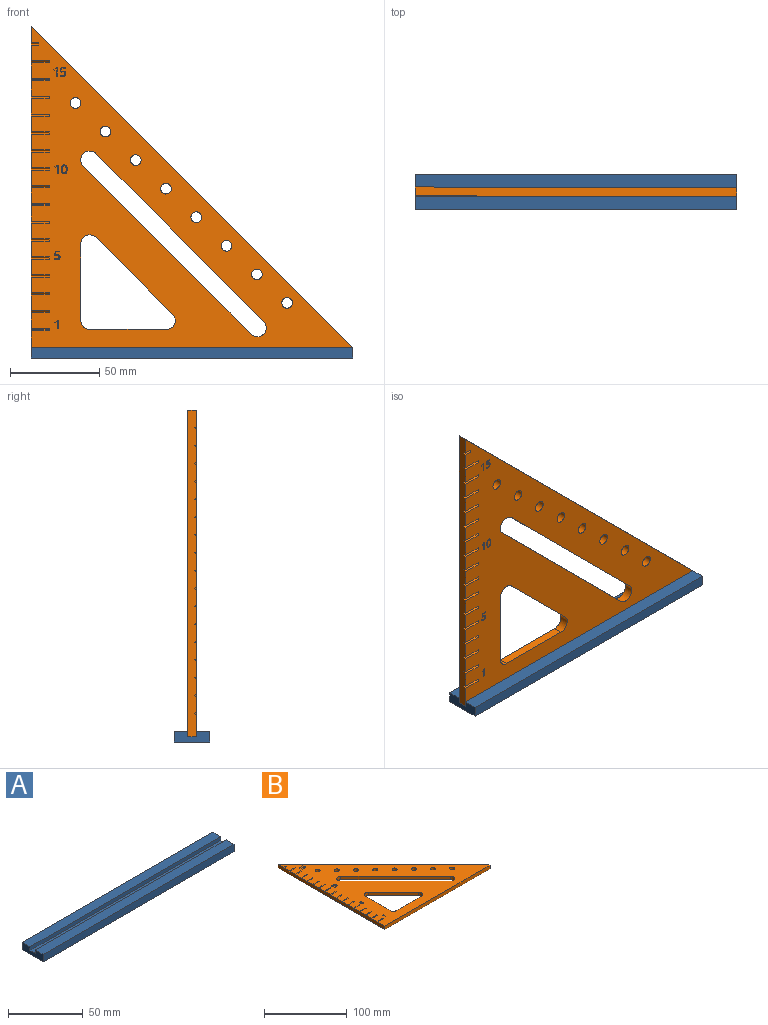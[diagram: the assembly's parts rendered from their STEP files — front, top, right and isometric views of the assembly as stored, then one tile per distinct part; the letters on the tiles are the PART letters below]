
ASSEMBLY  parts=2 mates=1
PART A: 10 faces, bbox 180x20x6 mm
  f0: plane 180x20mm, normal (0,0,-1), area 3600mm2, adj f1,f7,f8,f9
  f1: plane 180x6mm, normal (0,1,0), area 1080mm2, adj f0,f2,f8,f9
  f2: plane 180x7.5mm, normal (0,0,1), area 1350mm2, adj f1,f3,f8,f9
  f3: plane 180x3mm, normal (0,-1,0), area 540mm2, adj f2,f4,f8,f9
  f4: plane 180x5mm, normal (0,0,1), area 900mm2, adj f3,f5,f8,f9
  f5: plane 180x3mm, normal (0,1,0), area 540mm2, adj f4,f6,f8,f9
  f6: plane 180x7.5mm, normal (0,0,1), area 1350mm2, adj f5,f7,f8,f9
  f7: plane 180x6mm, normal (0,-1,0), area 1080mm2, adj f0,f6,f8,f9
  f8: plane 20x6mm, normal (1,0,0), area 105mm2, adj f0,f1,f2,f3,f4,f5,f6,f7
  f9: plane 20x6mm, normal (-1,0,0), area 105mm2, adj f0,f1,f2,f3,f4,f5,f6,f7
PART B: 164 faces, bbox 180x183x5 mm
  f0: plane 183x180mm, normal (0,0,1), area 13110.9mm2, adj f1,f2,f3,f4,f5,f6,f7,f8
  f1: plane 183x5mm, normal (-1,0,0), area 899.5mm2, adj f0,f12,f14,f16,f17,f18,f20,f21
  f2: cylinder r=5mm len=8.54mm, axis (0,0,-1), area 58.9mm2, adj f0,f3,f15,f16
  f3: plane 42.93x5mm, normal (0,1,0), area 214.6mm2, adj f0,f2,f4,f16
  f4: cylinder r=5mm len=5mm, axis (0,0,-1), area 39.3mm2, adj f0,f3,f5,f16
  f5: plane 42.93x5mm, normal (1,0,0), area 214.6mm2, adj f0,f4,f6,f16
  f6: cylinder r=5mm len=8.54mm, axis (0,0,-1), area 58.9mm2, adj f0,f5,f15,f16
  f7: plane 94.05x94.05mm, normal (0.71,0.71,0), area 665mm2, adj f0,f8,f13,f16
  f8: cylinder r=5mm len=8.54mm, axis (0,0,-1), area 78.5mm2, adj f0,f7,f9,f16
  f9: plane 94.05x94.05mm, normal (-0.71,-0.71,0), area 665mm2, adj f0,f8,f13,f16
  f10: plane 5x3mm, normal (1,0,0), area 15mm2, adj f0,f11,f14,f16
  f11: plane 5x0mm, normal (0,-1,0), area 0mm2, adj f0,f10,f12,f16
  f12: plane 180x180mm, normal (0.71,0.71,0), area 1272.8mm2, adj f0,f1,f11,f16
  f13: cylinder r=5mm len=8.54mm, axis (0,0,-1), area 78.5mm2, adj f0,f7,f9,f16
  f14: plane 180x5mm, normal (0,-1,0), area 900mm2, adj f0,f1,f10,f16
  f15: plane 42.93x42.93mm, normal (-0.71,-0.71,0), area 303.6mm2, adj f0,f2,f6,f16
  f16: plane 183x180mm, normal (0,0,-1), area 13372.4mm2, adj f1,f2,f3,f4,f5,f6,f7,f8
  f17: plane 10x1.31mm, normal (0,-0.88,0.47), area 14.9mm2, adj f0,f1,f18,f19
  f18: plane 10x1.31mm, normal (0,0.88,0.47), area 14.9mm2, adj f0,f1,f17,f19
  f19: plane 1.39x1.31mm, normal (-1,0,0), area 0.9mm2, adj f0,f17,f18
  f20: plane 10x1.31mm, normal (0,-0.88,0.47), area 14.9mm2, adj f0,f1,f21,f22
  f21: plane 10x1.31mm, normal (0,0.88,0.47), area 14.9mm2, adj f0,f1,f20,f22
  f22: plane 1.39x1.31mm, normal (-1,0,0), area 0.9mm2, adj f0,f20,f21
  f23: plane 10x1.31mm, normal (0,-0.88,0.47), area 14.9mm2, adj f0,f1,f24,f25
  f24: plane 10x1.31mm, normal (0,0.88,0.47), area 14.9mm2, adj f0,f1,f23,f25
  f25: plane 1.39x1.31mm, normal (-1,0,0), area 0.9mm2, adj f0,f23,f24
  f26: plane 10x1.31mm, normal (0,-0.88,0.47), area 14.9mm2, adj f0,f1,f27,f28
  f27: plane 10x1.31mm, normal (0,0.88,0.47), area 14.9mm2, adj f0,f1,f26,f28
  f28: plane 1.39x1.31mm, normal (-1,0,0), area 0.9mm2, adj f0,f26,f27
  f29: plane 10x1.31mm, normal (0,-0.88,0.47), area 14.9mm2, adj f0,f1,f30,f31
  f30: plane 10x1.31mm, normal (0,0.88,0.47), area 14.9mm2, adj f0,f1,f29,f31
  f31: plane 1.39x1.31mm, normal (-1,0,0), area 0.9mm2, adj f0,f29,f30
  f32: plane 10x1.31mm, normal (0,-0.88,0.47), area 14.9mm2, adj f0,f1,f33,f34
  f33: plane 10x1.31mm, normal (0,0.88,0.47), area 14.9mm2, adj f0,f1,f32,f34
  f34: plane 1.39x1.31mm, normal (-1,0,0), area 0.9mm2, adj f0,f32,f33
  f35: plane 10x1.31mm, normal (0,-0.88,0.47), area 14.9mm2, adj f0,f1,f36,f37
  f36: plane 10x1.31mm, normal (0,0.88,0.47), area 14.9mm2, adj f0,f1,f35,f37
  f37: plane 1.39x1.31mm, normal (-1,0,0), area 0.9mm2, adj f0,f35,f36
  f38: plane 10x1.31mm, normal (0,-0.88,0.47), area 14.9mm2, adj f0,f1,f39,f40
  f39: plane 10x1.31mm, normal (0,0.88,0.47), area 14.9mm2, adj f0,f1,f38,f40
  f40: plane 1.39x1.31mm, normal (-1,0,0), area 0.9mm2, adj f0,f38,f39
  f41: plane 10x1.31mm, normal (0,-0.88,0.47), area 14.9mm2, adj f0,f1,f42,f43
  f42: plane 10x1.31mm, normal (0,0.88,0.47), area 14.9mm2, adj f0,f1,f41,f43
  f43: plane 1.39x1.31mm, normal (-1,0,0), area 0.9mm2, adj f0,f41,f42
  f44: plane 10x1.31mm, normal (0,-0.88,0.47), area 14.9mm2, adj f0,f1,f45,f46
  f45: plane 10x1.31mm, normal (0,0.88,0.47), area 14.9mm2, adj f0,f1,f44,f46
  f46: plane 1.39x1.31mm, normal (-1,0,0), area 0.9mm2, adj f0,f44,f45
  f47: plane 10x1.31mm, normal (0,-0.88,0.47), area 14.9mm2, adj f0,f1,f48,f49
  f48: plane 10x1.31mm, normal (0,0.88,0.47), area 14.9mm2, adj f0,f1,f47,f49
  f49: plane 1.39x1.31mm, normal (-1,0,0), area 0.9mm2, adj f0,f47,f48
  f50: plane 10x1.31mm, normal (0,-0.88,0.47), area 14.9mm2, adj f0,f1,f51,f52
  f51: plane 10x1.31mm, normal (0,0.88,0.47), area 14.9mm2, adj f0,f1,f50,f52
  f52: plane 1.39x1.31mm, normal (-1,0,0), area 0.9mm2, adj f0,f50,f51
  f53: plane 10x1.31mm, normal (0,-0.88,0.47), area 14.9mm2, adj f0,f1,f54,f55
  f54: plane 10x1.31mm, normal (0,0.88,0.47), area 14.9mm2, adj f0,f1,f53,f55
  f55: plane 1.39x1.31mm, normal (-1,0,0), area 0.9mm2, adj f0,f53,f54
  f56: plane 10x1.31mm, normal (0,-0.88,0.47), area 14.9mm2, adj f0,f1,f57,f58
  f57: plane 10x1.31mm, normal (0,0.88,0.47), area 14.9mm2, adj f0,f1,f56,f58
  f58: plane 1.39x1.31mm, normal (-1,0,0), area 0.9mm2, adj f0,f56,f57
  f59: plane 10x1.31mm, normal (0,-0.88,0.47), area 14.9mm2, adj f0,f1,f60,f61
  f60: plane 10x1.31mm, normal (0,0.88,0.47), area 14.9mm2, adj f0,f1,f59,f61
  f61: plane 1.39x1.31mm, normal (-1,0,0), area 0.9mm2, adj f0,f59,f60
  f62: plane 10x1.31mm, normal (0,0.88,0.47), area 14.9mm2, adj f0,f1,f63,f64
  f63: plane 10x1.31mm, normal (0,-0.88,0.47), area 14.9mm2, adj f0,f1,f62,f64
  f64: plane 1.39x1.31mm, normal (-1,0,0), area 0.9mm2, adj f0,f62,f63
  f65: plane 4x1.31mm, normal (0,-0.88,0.47), area 5.9mm2, adj f0,f1,f66,f67
  f66: plane 4x1.31mm, normal (0,0.88,0.47), area 5.9mm2, adj f0,f1,f65,f67
  f67: plane 1.39x1.31mm, normal (-1,0,0), area 0.9mm2, adj f0,f65,f66
  f68: cylinder r=3mm len=6mm, axis (0,0,1), area 94.2mm2, adj f0,f16
  f69: extruded ~1.86x1mm, area 1.9mm2, adj f0,f70,f84,f85
  f70: extruded ~1.2x1mm, area 1.4mm2, adj f0,f69,f71,f85
  f71: extruded ~1.21x1mm, area 1.4mm2, adj f0,f70,f72,f85
  f72: extruded ~1.89x1mm, area 2mm2, adj f0,f71,f73,f85
  f73: extruded ~1.87x1mm, area 1.9mm2, adj f0,f72,f74,f85
  f74: extruded ~1.2x1mm, area 1.4mm2, adj f0,f73,f75,f85
  f75: extruded ~1.22x1mm, area 1.4mm2, adj f0,f74,f84,f85
  f76: extruded ~1.54x1mm, area 1.6mm2, adj f77,f83,f85,f86
  f77: extruded ~1x0.8mm, area 1mm2, adj f76,f78,f85,f86
  f78: extruded ~1x0.8mm, area 1mm2, adj f77,f79,f85,f86
  f79: extruded ~1.54x1mm, area 1.6mm2, adj f78,f80,f85,f86
  f80: extruded ~1.54x1mm, area 1.6mm2, adj f79,f81,f85,f86
  f81: extruded ~1x0.8mm, area 1mm2, adj f80,f82,f85,f86
  f82: extruded ~1x0.8mm, area 1mm2, adj f81,f83,f85,f86
  f83: extruded ~1.55x1mm, area 1.6mm2, adj f76,f82,f85,f86
  f84: extruded ~1.89x1mm, area 2mm2, adj f0,f69,f75,f85
  f85: plane 5.01x3.22mm, normal (0,0,1), area 6.3mm2, adj f69,f70,f71,f72,f73,f74,f75,f76
  f86: plane 4.06x2.09mm, normal (0,0,1), area 7.2mm2, adj f76,f77,f78,f79,f80,f81,f82,f83
  f87: extruded ~1x0.76mm, area 0.8mm2, adj f0,f88,f105,f106
  f88: plane 1.46x1mm, normal (-1,0.08,0), area 1.5mm2, adj f0,f87,f89,f106
  f89: plane 1.95x1mm, normal (0,1,0), area 1.9mm2, adj f0,f88,f90,f106
  f90: plane 1x0.51mm, normal (-1,0,0), area 0.5mm2, adj f0,f89,f91,f106
  f91: plane 2.42x1mm, normal (0,-1,0), area 2.4mm2, adj f0,f90,f92,f106
  f92: plane 2.28x1mm, normal (1,-0.08,0), area 2.3mm2, adj f0,f91,f93,f106
  f93: plane 1x0.29mm, normal (0.54,0.84,0), area 0.3mm2, adj f0,f92,f94,f106
  f94: extruded ~1x0.85mm, area 0.9mm2, adj f0,f93,f95,f106
  f95: extruded ~1.25x1.02mm, area 1.8mm2, adj f0,f94,f96,f106
  f96: extruded ~1x0.8mm, area 0.9mm2, adj f0,f95,f97,f106
  f97: extruded ~1x0.91mm, area 1mm2, adj f0,f96,f98,f106
  f98: extruded ~1x0.68mm, area 0.7mm2, adj f0,f97,f99,f106
  f99: extruded ~1x0.58mm, area 0.6mm2, adj f0,f98,f100,f106
  f100: plane 1x0.53mm, normal (1,0,0), area 0.5mm2, adj f0,f99,f101,f106
  f101: extruded ~1.26x1mm, area 1.3mm2, adj f0,f100,f102,f106
  f102: extruded ~1.33x1mm, area 1.4mm2, adj f0,f101,f103,f106
  f103: extruded ~1.19x1mm, area 1.3mm2, adj f0,f102,f104,f106
  f104: extruded ~1.04x1mm, area 1.2mm2, adj f0,f103,f105,f106
  f105: extruded ~1.21x1mm, area 1.3mm2, adj f0,f87,f104,f106
  f106: plane 4.94x3.06mm, normal (0,0,1), area 5.5mm2, adj f87,f88,f89,f90,f91,f92,f93,f94
  f107: plane 4.87x1mm, normal (-1,0,0), area 4.9mm2, adj f0,f108,f115,f116
  f108: plane 1x0.47mm, normal (0,-1,0), area 0.5mm2, adj f0,f107,f109,f116
  f109: plane 1.29x1mm, normal (0.61,-0.79,0), area 1.6mm2, adj f0,f108,f110,f116
  f110: plane 1x0.38mm, normal (0.79,0.61,0), area 0.5mm2, adj f0,f109,f111,f116
  f111: extruded ~1x0.79mm, area 1mm2, adj f0,f110,f112,f116
  f112: extruded ~1x0.16mm, area 0.2mm2, adj f0,f111,f113,f116
  f113: extruded ~1x0.82mm, area 0.8mm2, adj f0,f112,f114,f116
  f114: plane 3.47x1mm, normal (1,0,0), area 3.5mm2, adj f0,f113,f115,f116
  f115: plane 1x0.54mm, normal (0,1,0), area 0.5mm2, adj f0,f107,f114,f116
  f116: plane 4.87x1.75mm, normal (0,0,1), area 3.2mm2, adj f107,f108,f109,f110,f111,f112,f113,f114
  f117: plane 4.87x1mm, normal (-1,0,0), area 4.9mm2, adj f0,f118,f125,f126
  f118: plane 1x0.47mm, normal (0,-1,0), area 0.5mm2, adj f0,f117,f119,f126
  f119: plane 1.29x1mm, normal (0.61,-0.79,0), area 1.6mm2, adj f0,f118,f120,f126
  f120: plane 1x0.38mm, normal (0.79,0.61,0), area 0.5mm2, adj f0,f119,f121,f126
  f121: extruded ~1x0.79mm, area 1mm2, adj f0,f120,f122,f126
  f122: extruded ~1x0.16mm, area 0.2mm2, adj f0,f121,f123,f126
  f123: extruded ~1x0.82mm, area 0.8mm2, adj f0,f122,f124,f126
  f124: plane 3.47x1mm, normal (1,0,0), area 3.5mm2, adj f0,f123,f125,f126
  f125: plane 1x0.54mm, normal (0,1,0), area 0.5mm2, adj f0,f117,f124,f126
  f126: plane 4.87x1.75mm, normal (0,0,1), area 3.2mm2, adj f117,f118,f119,f120,f121,f122,f123,f124
  f127: extruded ~1x0.76mm, area 0.8mm2, adj f0,f128,f145,f146
  f128: plane 1.46x1mm, normal (-1,0.08,0), area 1.5mm2, adj f0,f127,f129,f146
  f129: plane 1.95x1mm, normal (0,1,0), area 1.9mm2, adj f0,f128,f130,f146
  f130: plane 1x0.51mm, normal (-1,0,0), area 0.5mm2, adj f0,f129,f131,f146
  f131: plane 2.42x1mm, normal (0,-1,0), area 2.4mm2, adj f0,f130,f132,f146
  f132: plane 2.28x1mm, normal (1,-0.08,0), area 2.3mm2, adj f0,f131,f133,f146
  f133: plane 1x0.29mm, normal (0.54,0.84,0), area 0.3mm2, adj f0,f132,f134,f146
  f134: extruded ~1x0.85mm, area 0.9mm2, adj f0,f133,f135,f146
  f135: extruded ~1.25x1.02mm, area 1.8mm2, adj f0,f134,f136,f146
  f136: extruded ~1x0.8mm, area 0.9mm2, adj f0,f135,f137,f146
  f137: extruded ~1x0.91mm, area 1mm2, adj f0,f136,f138,f146
  f138: extruded ~1x0.68mm, area 0.7mm2, adj f0,f137,f139,f146
  f139: extruded ~1x0.58mm, area 0.6mm2, adj f0,f138,f140,f146
  f140: plane 1x0.53mm, normal (1,0,0), area 0.5mm2, adj f0,f139,f141,f146
  f141: extruded ~1.26x1mm, area 1.3mm2, adj f0,f140,f142,f146
  f142: extruded ~1.33x1mm, area 1.4mm2, adj f0,f141,f143,f146
  f143: extruded ~1.19x1mm, area 1.3mm2, adj f0,f142,f144,f146
  f144: extruded ~1.04x1mm, area 1.2mm2, adj f0,f143,f145,f146
  f145: extruded ~1.21x1mm, area 1.3mm2, adj f0,f127,f144,f146
  f146: plane 4.94x3.06mm, normal (0,0,1), area 5.5mm2, adj f127,f128,f129,f130,f131,f132,f133,f134
  f147: plane 4.87x1mm, normal (-1,0,0), area 4.9mm2, adj f0,f148,f155,f156
  f148: plane 1x0.47mm, normal (0,-1,0), area 0.5mm2, adj f0,f147,f149,f156
  f149: plane 1.29x1mm, normal (0.61,-0.79,0), area 1.6mm2, adj f0,f148,f150,f156
  f150: plane 1x0.38mm, normal (0.79,0.61,0), area 0.5mm2, adj f0,f149,f151,f156
  f151: extruded ~1x0.79mm, area 1mm2, adj f0,f150,f152,f156
  f152: extruded ~1x0.16mm, area 0.2mm2, adj f0,f151,f153,f156
  f153: extruded ~1x0.82mm, area 0.8mm2, adj f0,f152,f154,f156
  f154: plane 3.47x1mm, normal (1,0,0), area 3.5mm2, adj f0,f153,f155,f156
  f155: plane 1x0.54mm, normal (0,1,0), area 0.5mm2, adj f0,f147,f154,f156
  f156: plane 4.87x1.75mm, normal (0,0,1), area 3.2mm2, adj f147,f148,f149,f150,f151,f152,f153,f154
  f157: cylinder r=3mm len=6mm, axis (0,0,1), area 94.2mm2, adj f0,f16
  f158: cylinder r=3mm len=6mm, axis (0,0,1), area 94.2mm2, adj f0,f16
  f159: cylinder r=3mm len=6mm, axis (0,0,1), area 94.2mm2, adj f0,f16
  f160: cylinder r=3mm len=6mm, axis (0,0,1), area 94.2mm2, adj f0,f16
  f161: cylinder r=3mm len=6mm, axis (0,0,1), area 94.2mm2, adj f0,f16
  f162: cylinder r=3mm len=6mm, axis (0,0,1), area 94.2mm2, adj f0,f16
  f163: cylinder r=3mm len=6mm, axis (0,0,1), area 94.2mm2, adj f0,f16
PLACE A t=(-95.28,-32.98,-47.79)mm
PLACE B rot(axis=(1,0,0),90deg) t=(-39.87,-32.98,30.69)mm
MATE fastened B.f14 <-> A.f4  axis (0,0,-1) through (-5.28,-32.98,-44.79)mm
